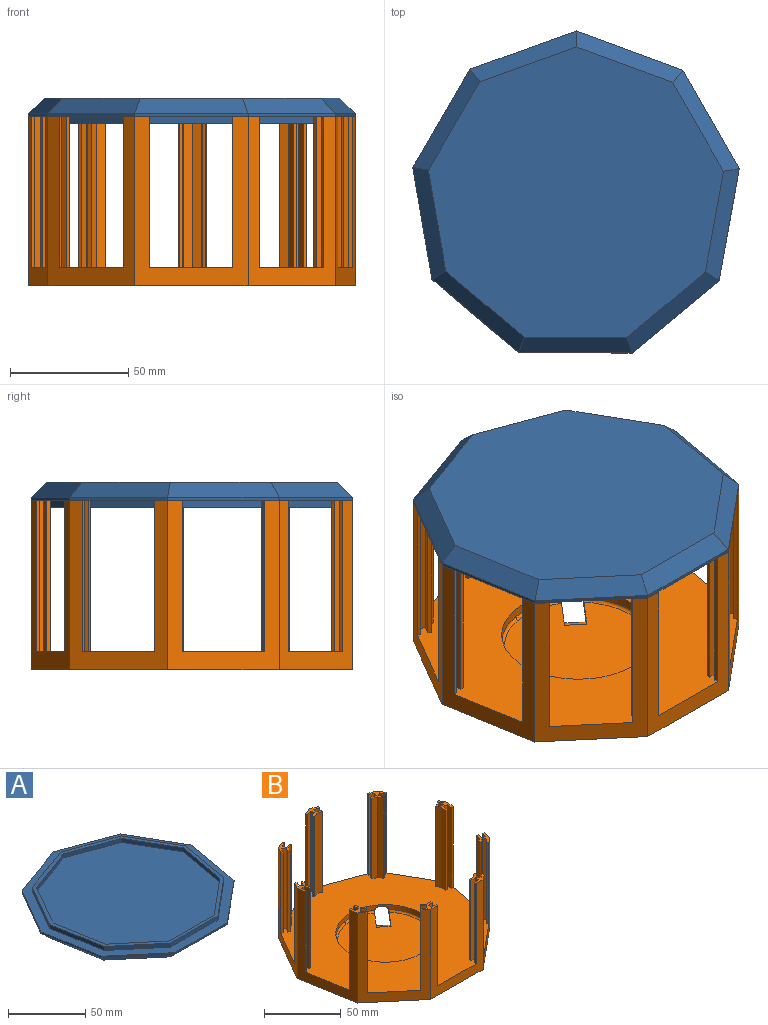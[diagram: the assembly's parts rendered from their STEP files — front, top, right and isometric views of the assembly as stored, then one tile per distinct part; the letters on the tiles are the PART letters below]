
ASSEMBLY  parts=2 mates=2
PART A: 40 faces, bbox 137.9x135.9x10.8 mm
  f0: plane 137.87x135.87mm, normal (0,0,1), area 2603.3mm2, adj f1,f2,f3,f4,f5,f6,f7,f8
  f1: plane 41.38x24.1mm, normal (-0.86,0.5,0), area 60.8mm2, adj f0,f2,f9,f38
  f2: plane 47.19x8.14mm, normal (-0.99,-0.17,0), area 60.8mm2, adj f0,f1,f3,f39
  f3: plane 36.56x30.92mm, normal (-0.65,-0.76,0), area 60.8mm2, adj f0,f2,f4,f37
  f4: plane 47.88x1.27mm, normal (0,-1,0), area 60.8mm2, adj f0,f3,f5,f35
  f5: plane 36.8x30.64mm, normal (0.64,-0.77,0), area 60.8mm2, adj f0,f4,f6,f33
  f6: plane 47.12x8.49mm, normal (0.98,-0.18,0), area 60.8mm2, adj f0,f5,f7,f31
  f7: plane 41.56x23.78mm, normal (0.87,0.5,0), area 60.8mm2, adj f0,f6,f8,f32
  f8: plane 44.93x16.55mm, normal (0.35,0.94,0), area 60.8mm2, adj f0,f7,f9,f34
  f9: plane 45.06x16.21mm, normal (-0.34,0.94,0), area 60.8mm2, adj f0,f1,f8,f36
  f10: plane 124.56x122.75mm, normal (0,0,-1), area 11569.2mm2, adj f31,f32,f33,f34,f35,f36,f37,f38
  f11: plane 40.78x7.19mm, normal (0.98,0.17,0), area 131.5mm2, adj f12,f28,f29,f30
  f12: plane 35.87x20.71mm, normal (0.87,-0.5,0), area 131.5mm2, adj f11,f13,f29,f30
  f13: plane 38.92x14.16mm, normal (0.34,-0.94,0), area 131.5mm2, adj f12,f14,f29,f30
  f14: plane 38.92x14.16mm, normal (-0.34,-0.94,0), area 131.5mm2, adj f13,f15,f29,f30
  f15: plane 35.87x20.71mm, normal (-0.87,-0.5,0), area 131.5mm2, adj f14,f16,f29,f30
  f16: plane 40.78x7.19mm, normal (-0.98,0.17,0), area 131.5mm2, adj f15,f17,f29,f30
  f17: plane 31.73x26.62mm, normal (-0.64,0.77,0), area 131.5mm2, adj f16,f18,f29,f30
  f18: plane 41.41x3.18mm, normal (0,1,0), area 131.5mm2, adj f17,f28,f29,f30
  f19: plane 37.47x21.63mm, normal (-0.87,0.5,0), area 137.4mm2, adj f0,f20,f27,f29
  f20: plane 42.61x7.51mm, normal (-0.98,-0.17,0), area 137.4mm2, adj f0,f19,f21,f29
  f21: plane 33.14x27.81mm, normal (-0.64,-0.77,0), area 137.4mm2, adj f0,f20,f22,f29
  f22: plane 43.26x3.18mm, normal (0,-1,0), area 137.4mm2, adj f0,f21,f23,f29
  f23: plane 33.14x27.81mm, normal (0.64,-0.77,0), area 137.4mm2, adj f0,f22,f24,f29
  f24: plane 42.61x7.51mm, normal (0.98,-0.17,0), area 137.4mm2, adj f0,f23,f25,f29
  f25: plane 37.47x21.63mm, normal (0.87,0.5,0), area 137.4mm2, adj f0,f24,f26,f29
  f26: plane 40.65x14.8mm, normal (0.34,0.94,0), area 137.4mm2, adj f0,f25,f27,f29
  f27: plane 40.65x14.8mm, normal (-0.34,0.94,0), area 137.4mm2, adj f0,f19,f26,f29
  f28: plane 31.73x26.62mm, normal (0.64,0.77,0), area 131.5mm2, adj f11,f18,f29,f30
  f29: plane 124.57x122.68mm, normal (0,0,1), area 967.9mm2, adj f11,f12,f13,f14,f15,f16,f17,f18
  f30: plane 119.25x117.43mm, normal (0,0,1), area 10602.5mm2, adj f11,f12,f13,f14,f15,f16,f17,f18
  f31: plane 47.12x14.33mm, normal (0.7,-0.13,-0.71), area 409.2mm2, adj f6,f10,f32,f33
  f32: plane 42.71x28.15mm, normal (0.61,0.35,-0.71), area 409.2mm2, adj f7,f10,f31,f34
  f33: plane 39.08x34.04mm, normal (0.45,-0.54,-0.71), area 409.2mm2, adj f5,f10,f31,f35
  f34: plane 44.96x21.71mm, normal (0.24,0.66,-0.71), area 409.2mm2, adj f8,f10,f32,f36
  f35: plane 47.88x6.52mm, normal (0,-0.71,-0.71), area 409.2mm2, adj f4,f10,f33,f37
  f36: plane 45.06x21.4mm, normal (-0.24,0.67,-0.71), area 409.2mm2, adj f9,f10,f34,f38
  f37: plane 38.9x34.27mm, normal (-0.46,-0.54,-0.71), area 409.2mm2, adj f3,f10,f35,f39
  f38: plane 42.58x28.42mm, normal (-0.61,0.36,-0.71), area 409.2mm2, adj f1,f10,f36,f39
  f39: plane 47.19x14mm, normal (-0.7,-0.12,-0.71), area 409.2mm2, adj f2,f10,f37,f38
PART B: 137 faces, bbox 137.9x135.9x71.6 mm
  f0: plane 64x1.43mm, normal (-0.5,-0.86,0), area 105.7mm2, adj f18,f38,f46,f129
  f1: plane 64x1.55mm, normal (0.94,0.34,0), area 105.7mm2, adj f18,f37,f38,f134
  f2: plane 64x1.43mm, normal (0.5,0.86,0), area 105.7mm2, adj f19,f30,f38,f126
  f3: plane 64x1.63mm, normal (0.17,-0.99,0), area 105.7mm2, adj f19,f38,f52,f124
  f4: plane 64x1.63mm, normal (-0.17,0.99,0), area 105.7mm2, adj f20,f31,f38,f122
  f5: plane 64x1.26mm, normal (0.76,-0.65,0), area 105.7mm2, adj f20,f38,f56,f117
  f6: plane 64x1.26mm, normal (-0.76,0.65,0), area 105.7mm2, adj f21,f32,f38,f116
  f7: plane 64x1.65mm, normal (1,0,0), area 105.7mm2, adj f21,f38,f60,f111
  f8: plane 64x1.65mm, normal (-1,0,0), area 105.7mm2, adj f22,f33,f38,f107
  f9: plane 64x1.27mm, normal (0.77,0.64,0), area 105.7mm2, adj f22,f38,f64,f108
  f10: plane 64x1.27mm, normal (-0.77,-0.64,0), area 105.7mm2, adj f23,f34,f38,f104
  f11: plane 64x1.63mm, normal (0.18,0.98,0), area 105.7mm2, adj f23,f38,f68,f99
  f12: plane 64x1.63mm, normal (-0.18,-0.98,0), area 105.7mm2, adj f24,f35,f38,f98
  f13: plane 64x1.43mm, normal (-0.5,0.87,0), area 105.7mm2, adj f24,f38,f72,f93
  f14: plane 64x1.43mm, normal (0.5,-0.87,0), area 105.7mm2, adj f25,f27,f38,f92
  f15: plane 64x1.55mm, normal (-0.94,0.35,0), area 105.7mm2, adj f25,f38,f76,f87
  f16: plane 64x1.55mm, normal (0.94,-0.35,0), area 105.7mm2, adj f26,f36,f38,f83
  f17: plane 64x1.55mm, normal (-0.94,-0.34,0), area 105.7mm2, adj f26,f38,f80,f84
  f18: plane 11.32x10.83mm, normal (0,0,1), area 40.2mm2, adj f0,f1,f30,f37,f45,f46,f47,f48
  f19: plane 11.75x8.68mm, normal (0,0,1), area 40.2mm2, adj f2,f3,f30,f31,f49,f50,f51,f52
  f20: plane 11.44x10.03mm, normal (0,0,1), area 40.2mm2, adj f4,f5,f31,f32,f53,f54,f55,f56
  f21: plane 11.22x8.97mm, normal (0,0,1), area 40.2mm2, adj f6,f7,f32,f33,f57,f58,f59,f60
  f22: plane 11.23x8.94mm, normal (0,0,1), area 40.2mm2, adj f8,f9,f33,f34,f61,f62,f63,f64
  f23: plane 11.44x10.07mm, normal (0,0,1), area 40.2mm2, adj f10,f11,f34,f35,f65,f66,f67,f68
  f24: plane 11.76x8.67mm, normal (0,0,1), area 40.2mm2, adj f12,f13,f27,f35,f69,f70,f71,f72
  f25: plane 11.31x10.86mm, normal (0,0,1), area 40.2mm2, adj f14,f15,f27,f36,f73,f74,f75,f76
  f26: plane 11.93x8.15mm, normal (0,0,1), area 40.2mm2, adj f16,f17,f36,f37,f77,f78,f79,f80
  f27: plane 71.62x41.56mm, normal (0.87,0.5,0), area 1146.5mm2, adj f14,f24,f25,f35,f36,f38,f39,f40
  f28: cylinder r=32.38mm len=64.77mm, axis (0,0,1), area 757.1mm2, adj f38,f40,f43,f44,f135
  f29: plane 62.23x62.23mm, normal (0,0,1), area 2885.8mm2, adj f41,f42,f135,f136
  f30: plane 71.62x41.38mm, normal (-0.86,0.5,0), area 1177.7mm2, adj f2,f18,f19,f31,f37,f38,f39,f45
  f31: plane 71.62x47.19mm, normal (-0.99,-0.17,0), area 1177.7mm2, adj f4,f19,f20,f30,f32,f38,f39,f51
  f32: plane 71.62x36.56mm, normal (-0.65,-0.76,0), area 1177.7mm2, adj f6,f20,f21,f31,f33,f38,f39,f55
  f33: plane 71.62x47.88mm, normal (0,-1,0), area 1177.7mm2, adj f8,f21,f22,f32,f34,f38,f39,f59
  f34: plane 71.62x36.8mm, normal (0.64,-0.77,0), area 1177.7mm2, adj f10,f22,f23,f33,f35,f38,f39,f63
  f35: plane 71.62x47.12mm, normal (0.98,-0.18,0), area 1177.7mm2, adj f12,f23,f24,f27,f34,f38,f39,f67
  f36: plane 71.62x44.93mm, normal (0.35,0.94,0), area 1151.1mm2, adj f16,f25,f26,f27,f37,f38,f39,f40
  f37: plane 71.62x45.06mm, normal (-0.34,0.94,0), area 1177.7mm2, adj f1,f18,f26,f30,f36,f38,f39,f79
  f38: plane 135.67x133.7mm, normal (0,0,1), area 10517.3mm2, adj f0,f1,f2,f3,f4,f5,f6,f7
  f39: plane 137.87x135.87mm, normal (0,0,-1), area 13696.7mm2, adj f27,f30,f31,f32,f33,f34,f35,f36
  f40: plane 29.68x25.58mm, normal (0,0,-1), area 71.3mm2, adj f27,f28,f36,f43,f44
  f41: plane 40.7x34.76mm, normal (-0.76,0.65,0), area 128mm2, adj f27,f29,f39,f43,f136
  f42: plane 40.85x34.89mm, normal (0.76,-0.65,0), area 128.5mm2, adj f29,f36,f39,f44,f136
  f43: cylinder r=3.81mm len=31.97mm, axis (-0.65,-0.76,0), area 218.7mm2, adj f27,f28,f40,f41,f135
  f44: cylinder r=3.81mm len=32.15mm, axis (0.65,0.76,0), area 219.9mm2, adj f28,f36,f40,f42,f135
  f45: plane 64x1.32mm, normal (-0.5,-0.86,0), area 97.5mm2, adj f18,f30,f38,f131
  f46: plane 64x3.49mm, normal (0.86,-0.5,0), area 258.5mm2, adj f0,f18,f38,f47
  f47: plane 64x3.8mm, normal (0.34,-0.94,0), area 258.5mm2, adj f18,f38,f46,f48
  f48: plane 64x1.43mm, normal (0.94,0.34,0), area 97.5mm2, adj f18,f38,f47,f133
  f49: plane 64x3.49mm, normal (0.86,-0.5,0), area 258.5mm2, adj f19,f38,f50,f52
  f50: plane 64x1.32mm, normal (0.5,0.86,0), area 97.5mm2, adj f19,f38,f49,f128
  f51: plane 64x1.5mm, normal (0.17,-0.99,0), area 97.5mm2, adj f19,f31,f38,f123
  f52: plane 64x3.98mm, normal (0.99,0.17,0), area 258.5mm2, adj f3,f19,f38,f49
  f53: plane 64x3.98mm, normal (0.99,0.17,0), area 258.5mm2, adj f20,f38,f54,f56
  f54: plane 64x1.5mm, normal (-0.17,0.99,0), area 97.5mm2, adj f20,f38,f53,f121
  f55: plane 64x1.16mm, normal (0.76,-0.65,0), area 97.5mm2, adj f20,f32,f38,f119
  f56: plane 64x3.08mm, normal (0.65,0.76,0), area 258.5mm2, adj f5,f20,f38,f53
  f57: plane 64x3.08mm, normal (0.65,0.76,0), area 258.5mm2, adj f21,f38,f58,f60
  f58: plane 64x1.16mm, normal (-0.76,0.65,0), area 97.5mm2, adj f21,f38,f57,f115
  f59: plane 64x1.52mm, normal (1,0,0), area 97.5mm2, adj f21,f33,f38,f113
  f60: plane 64x4.04mm, normal (0,1,0), area 258.5mm2, adj f7,f21,f38,f57
  f61: plane 64x4.04mm, normal (0,1,0), area 258.5mm2, adj f22,f38,f62,f64
  f62: plane 64x1.52mm, normal (-1,0,0), area 97.5mm2, adj f22,f38,f61,f106
  f63: plane 64x1.17mm, normal (0.77,0.64,0), area 97.5mm2, adj f22,f34,f38,f110
  f64: plane 64x3.1mm, normal (-0.64,0.77,0), area 258.5mm2, adj f9,f22,f38,f61
  f65: plane 64x3.1mm, normal (-0.64,0.77,0), area 258.5mm2, adj f23,f38,f66,f68
  f66: plane 64x1.17mm, normal (-0.77,-0.64,0), area 97.5mm2, adj f23,f38,f65,f103
  f67: plane 64x1.5mm, normal (0.18,0.98,0), area 97.5mm2, adj f23,f35,f38,f101
  f68: plane 64x3.97mm, normal (-0.98,0.18,0), area 258.5mm2, adj f11,f23,f38,f65
  f69: plane 64x3.97mm, normal (-0.98,0.18,0), area 258.5mm2, adj f24,f38,f70,f72
  f70: plane 64x1.5mm, normal (-0.18,-0.98,0), area 97.5mm2, adj f24,f38,f69,f97
  f71: plane 64x1.32mm, normal (-0.5,0.87,0), area 97.5mm2, adj f24,f27,f38,f95
  f72: plane 64x3.51mm, normal (-0.87,-0.5,0), area 258.5mm2, adj f13,f24,f38,f69
  f73: plane 64x3.51mm, normal (-0.87,-0.5,0), area 258.5mm2, adj f25,f38,f74,f76
  f74: plane 64x1.32mm, normal (0.5,-0.87,0), area 97.5mm2, adj f25,f38,f73,f91
  f75: plane 64x1.43mm, normal (-0.94,0.35,0), area 97.5mm2, adj f25,f36,f38,f89
  f76: plane 64x3.79mm, normal (-0.35,-0.94,0), area 258.5mm2, adj f15,f25,f38,f73
  f77: plane 64x3.79mm, normal (-0.35,-0.94,0), area 258.5mm2, adj f26,f38,f78,f80
  f78: plane 64x1.43mm, normal (0.94,-0.35,0), area 97.5mm2, adj f26,f38,f77,f82
  f79: plane 64x1.43mm, normal (-0.94,-0.34,0), area 97.5mm2, adj f26,f37,f38,f86
  f80: plane 64x3.8mm, normal (0.34,-0.94,0), area 258.5mm2, adj f17,f26,f38,f77
  f81: plane 64x2.98mm, normal (0.94,-0.35,0), area 203.2mm2, adj f26,f38,f82,f83
  f82: plane 64x3.81mm, normal (0.35,0.94,0), area 260.1mm2, adj f26,f38,f78,f81
  f83: plane 64x3.81mm, normal (-0.35,-0.94,0), area 260.1mm2, adj f16,f26,f38,f81
  f84: plane 64x3.82mm, normal (-0.34,0.94,0), area 260.1mm2, adj f17,f26,f38,f85
  f85: plane 64x2.99mm, normal (-0.94,-0.34,0), area 203.2mm2, adj f26,f38,f84,f86
  f86: plane 64x3.82mm, normal (0.34,-0.94,0), area 260.1mm2, adj f26,f38,f79,f85
  f87: plane 64x3.81mm, normal (0.35,0.94,0), area 260.1mm2, adj f15,f25,f38,f88
  f88: plane 64x2.98mm, normal (-0.94,0.35,0), area 203.2mm2, adj f25,f38,f87,f89
  f89: plane 64x3.81mm, normal (-0.35,-0.94,0), area 260.1mm2, adj f25,f38,f75,f88
  f90: plane 64x2.76mm, normal (0.5,-0.87,0), area 203.2mm2, adj f25,f38,f91,f92
  f91: plane 64x3.53mm, normal (0.87,0.5,0), area 260.1mm2, adj f25,f38,f74,f90
  f92: plane 64x3.53mm, normal (-0.87,-0.5,0), area 260.1mm2, adj f14,f25,f38,f90
  f93: plane 64x3.53mm, normal (0.87,0.5,0), area 260.1mm2, adj f13,f24,f38,f94
  f94: plane 64x2.76mm, normal (-0.5,0.87,0), area 203.2mm2, adj f24,f38,f93,f95
  f95: plane 64x3.53mm, normal (-0.87,-0.5,0), area 260.1mm2, adj f24,f38,f71,f94
  f96: plane 64x3.12mm, normal (-0.18,-0.98,0), area 203.2mm2, adj f24,f38,f97,f98
  f97: plane 64x4mm, normal (0.98,-0.18,0), area 260.1mm2, adj f24,f38,f70,f96
  f98: plane 64x4mm, normal (-0.98,0.18,0), area 260.1mm2, adj f12,f24,f38,f96
  f99: plane 64x4mm, normal (0.98,-0.18,0), area 260.1mm2, adj f11,f23,f38,f100
  f100: plane 64x3.12mm, normal (0.18,0.98,0), area 203.2mm2, adj f23,f38,f99,f101
  f101: plane 64x4mm, normal (-0.98,0.18,0), area 260.1mm2, adj f23,f38,f67,f100
  f102: plane 64x2.44mm, normal (-0.77,-0.64,0), area 203.2mm2, adj f23,f38,f103,f104
  f103: plane 64x3.12mm, normal (0.64,-0.77,0), area 260.1mm2, adj f23,f38,f66,f102
  f104: plane 64x3.12mm, normal (-0.64,0.77,0), area 260.1mm2, adj f10,f23,f38,f102
  f105: plane 64x3.18mm, normal (-1,0,0), area 203.2mm2, adj f22,f38,f106,f107
  f106: plane 64x4.06mm, normal (0,-1,0), area 260.1mm2, adj f22,f38,f62,f105
  f107: plane 64x4.06mm, normal (0,1,0), area 260.1mm2, adj f8,f22,f38,f105
  f108: plane 64x3.12mm, normal (0.64,-0.77,0), area 260.1mm2, adj f9,f22,f38,f109
  f109: plane 64x2.44mm, normal (0.77,0.64,0), area 203.2mm2, adj f22,f38,f108,f110
  f110: plane 64x3.12mm, normal (-0.64,0.77,0), area 260.1mm2, adj f22,f38,f63,f109
  f111: plane 64x4.06mm, normal (0,-1,0), area 260.1mm2, adj f7,f21,f38,f112
  f112: plane 64x3.18mm, normal (1,0,0), area 203.2mm2, adj f21,f38,f111,f113
  f113: plane 64x4.06mm, normal (0,1,0), area 260.1mm2, adj f21,f38,f59,f112
  f114: plane 64x2.42mm, normal (-0.76,0.65,0), area 203.2mm2, adj f21,f38,f115,f116
  f115: plane 64x3.1mm, normal (-0.65,-0.76,0), area 260.1mm2, adj f21,f38,f58,f114
  f116: plane 64x3.1mm, normal (0.65,0.76,0), area 260.1mm2, adj f6,f21,f38,f114
  f117: plane 64x3.1mm, normal (-0.65,-0.76,0), area 260.1mm2, adj f5,f20,f38,f118
  f118: plane 64x2.42mm, normal (0.76,-0.65,0), area 203.2mm2, adj f20,f38,f117,f119
  f119: plane 64x3.1mm, normal (0.65,0.76,0), area 260.1mm2, adj f20,f38,f55,f118
  f120: plane 64x3.13mm, normal (-0.17,0.99,0), area 203.2mm2, adj f20,f38,f121,f122
  f121: plane 64x4.01mm, normal (-0.99,-0.17,0), area 260.1mm2, adj f20,f38,f54,f120
  f122: plane 64x4.01mm, normal (0.99,0.17,0), area 260.1mm2, adj f4,f20,f38,f120
  f123: plane 64x4.01mm, normal (0.99,0.17,0), area 260.1mm2, adj f19,f38,f51,f125
  f124: plane 64x4.01mm, normal (-0.99,-0.17,0), area 260.1mm2, adj f3,f19,f38,f125
  f125: plane 64x3.13mm, normal (0.17,-0.99,0), area 203.2mm2, adj f19,f38,f123,f124
  f126: plane 64x3.51mm, normal (0.86,-0.5,0), area 260.1mm2, adj f2,f19,f38,f127
  f127: plane 64x2.74mm, normal (0.5,0.86,0), area 203.2mm2, adj f19,f38,f126,f128
  f128: plane 64x3.51mm, normal (-0.86,0.5,0), area 260.1mm2, adj f19,f38,f50,f127
  f129: plane 64x3.51mm, normal (-0.86,0.5,0), area 260.1mm2, adj f0,f18,f38,f130
  f130: plane 64x2.74mm, normal (-0.5,-0.86,0), area 203.2mm2, adj f18,f38,f129,f131
  f131: plane 64x3.51mm, normal (0.86,-0.5,0), area 260.1mm2, adj f18,f38,f45,f130
  f132: plane 64x2.99mm, normal (0.94,0.34,0), area 203.2mm2, adj f18,f38,f133,f134
  f133: plane 64x3.82mm, normal (-0.34,0.94,0), area 260.1mm2, adj f18,f38,f48,f132
  f134: plane 64x3.82mm, normal (0.34,-0.94,0), area 260.1mm2, adj f1,f18,f38,f132
  f135: torus R=31.12mm, axis (0,0,1), area 381.3mm2, adj f28,f29,f43,f44
  f136: cylinder r=5.08mm len=10.1mm, axis (-0.76,0.65,0), area 50.7mm2, adj f29,f39,f41,f42
PLACE A rot(axis=(0.99,0.17,0),180deg) t=(-5.7,8.95,65.18)mm
PLACE B t=(-5.7,8.95,-14.15)mm
MATE parallel A.f30 <-> B.f28  axis (0,0,-1) through (-5.7,8.95,57.56)mm
MATE parallel A.f9 <-> B.f33  axis (0,-1,0) through (-5.95,-56.83,58.19)mm
